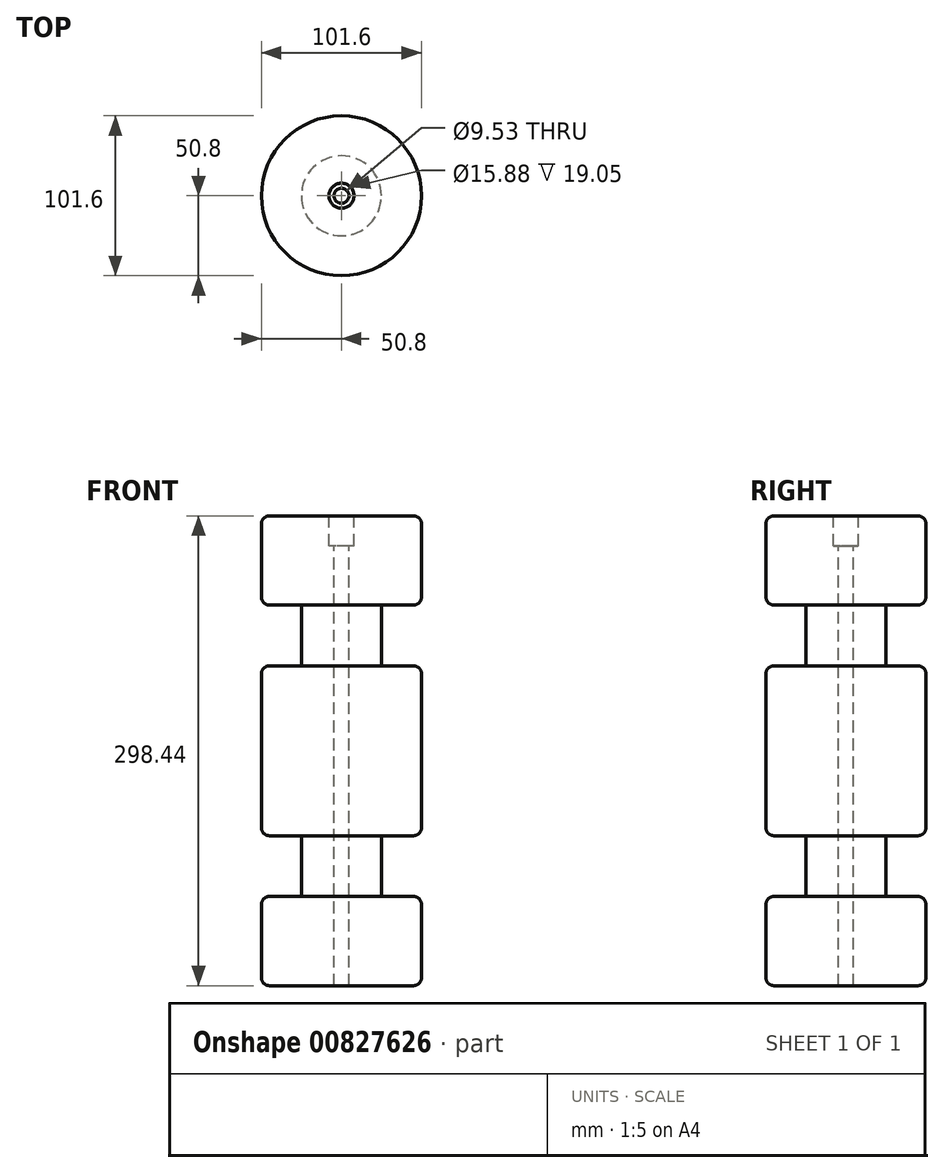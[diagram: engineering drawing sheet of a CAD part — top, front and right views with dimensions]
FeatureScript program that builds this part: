
annotation { "Feature Type Name" : "Feature", "Feature Type Description" : "" }
export const myFeature = defineFeature(function(context is Context, id is Id, definition is map)
    precondition{}
    {
        {
            var Q0;
            Q0=qCreatedBy(makeId("Front.planeOp"),FACE);
            var sketch = newSketch(context, id + "F0", { "sketchPlane" : qUnion([Q0])});
            skLineSegment(sketch, "E0.bottom", {"start": v(50.8, -53.98) * mm, "end": v(0, -53.98) * mm});
            skLineSegment(sketch, "E0.top", {"start": v(50.8, 149.22) * mm, "end": v(0, 149.22) * mm});
            skLineSegment(sketch, "E0.left", {"start": v(50.8, -53.98) * mm, "end": v(50.8, 16.34) * mm});
            skLineSegment(sketch, "E0.right", {"start": v(0, -53.98) * mm, "end": v(0, 149.22) * mm});
            skLineSegment(sketch, "E1.bottom", {"start": v(50.8, 92.54) * mm, "end": v(25.4, 92.54) * mm});
            skLineSegment(sketch, "E1.top", {"start": v(50.8, 16.34) * mm, "end": v(25.4, 16.34) * mm});
            skLineSegment(sketch, "E1.right", {"start": v(25.4, 92.54) * mm, "end": v(25.4, 16.34) * mm});
            skLineSegment(sketch, "E2.trimOffspring", {"start": v(50.8, 92.54) * mm, "end": v(50.8, 149.22) * mm});
            skSolve(sketch);
        }
        {
            var Q0;
            Q0=makeQuery(id+"F0.imprint","IMPRINT",FACE,{"disambiguationData":[TD([[makeQuery(id+"F0.imprint","IMPRINT",EDGE,{"derivedFrom":sQuery(id+"F0.wireOp",EDGE,"E0.bottom")}),-1.0]])]});
            var Q1;
            Q1=sQuery(id+"F0.wireOp",EDGE,"E0.right");
            revolve(context, id + "F1", {"surfaceOperationType" : NewSurfaceOperationType.NEW, "entities" : qUnion([Q0]), "axis" : qUnion([Q1]), "revolveType" : RevolveType.FULL});
        }
        {
            var Q0;
            Q0=makeQuery(id+"F1.opRevolve","SWEPT_EDGE",EDGE,{"disambiguationData":[OSD([sQuery(id+"F0.wireOp",EDGE,"E0.bottom"),sQuery(id+"F0.wireOp",EDGE,"E0.left")])]});
            var Q1;
            Q1=makeQuery(id+"F1.opRevolve","SWEPT_EDGE",EDGE,{"disambiguationData":[OSD([sQuery(id+"F0.wireOp",EDGE,"E0.left"),sQuery(id+"F0.wireOp",EDGE,"E1.top")])]});
            var Q2;
            Q2=makeQuery(id+"F1.opRevolve","SWEPT_EDGE",EDGE,{"disambiguationData":[OSD([sQuery(id+"F0.wireOp",EDGE,"E0.top"),sQuery(id+"F0.wireOp",EDGE,"E2.trimOffspring")])]});
            var Q3;
            Q3=makeQuery(id+"F1.opRevolve","SWEPT_EDGE",EDGE,{"disambiguationData":[OSD([sQuery(id+"F0.wireOp",EDGE,"E1.bottom"),sQuery(id+"F0.wireOp",EDGE,"E2.trimOffspring")])]});
            fillet(context, id + "F2", {"entities" : qUnion([Q0, Q1, Q2, Q3]), "radius" : 5.08 * mm, "tangentPropagation" : true, "allowEdgeOverflow" : false});
        }
        {
            var Q0;
            Q0=makeQuery(id+"F1.opRevolve","SWEPT_BODY",BODY,{"disambiguationData":[OSD([sQuery(id+"F0.wireOp",EDGE,"E0.bottom"),sQuery(id+"F0.wireOp",EDGE,"E0.top"),sQuery(id+"F0.wireOp",EDGE,"E0.left"),sQuery(id+"F0.wireOp",EDGE,"E0.right"),sQuery(id+"F0.wireOp",EDGE,"E1.bottom"),sQuery(id+"F0.wireOp",EDGE,"E1.top"),sQuery(id+"F0.wireOp",EDGE,"E1.right"),sQuery(id+"F0.wireOp",EDGE,"E2.trimOffspring")])]});
            var Q1;
            Q1=qCreatedBy(makeId("Top.planeOp"),FACE);
            mirror(context, id + "F3", {"operationType" : NewBodyOperationType.ADD, "entities" : qUnion([Q0]), "mirrorPlane" : qUnion([Q1])});
        }
        {
            var Q0;
            Q0=makeQuery(id+"F1.opRevolve","SWEPT_FACE",FACE,{"disambiguationData":[OSD([sQuery(id+"F0.wireOp",EDGE,"E0.top")])]});
            var sketch = newSketch(context, id + "F4", { "sketchPlane" : qUnion([Q0])});
            skCircle(sketch, "E3.0", {"center": v(0, 0) * mm, "radius": 45.72 * mm});
            skSolve(sketch);
        }
        {
            var Q0;
            Q0=sQuery(id+"F4.wireOp",VERTEX,"E3.0.center");
            var Q1;
            Q1=makeQuery(id+"F1.opRevolve","SWEPT_BODY",BODY,{"disambiguationData":[OSD([sQuery(id+"F0.wireOp",EDGE,"E0.bottom"),sQuery(id+"F0.wireOp",EDGE,"E0.top"),sQuery(id+"F0.wireOp",EDGE,"E0.left"),sQuery(id+"F0.wireOp",EDGE,"E0.right"),sQuery(id+"F0.wireOp",EDGE,"E1.bottom"),sQuery(id+"F0.wireOp",EDGE,"E1.top"),sQuery(id+"F0.wireOp",EDGE,"E1.right"),sQuery(id+"F0.wireOp",EDGE,"E2.trimOffspring")])]});
            hole(context, id + "F5", {"style" : HoleStyle.C_BORE, "endStyle" : HoleEndStyle.THROUGH, "standardTappedOrClearance" : lookupTablePath({ "standard" : "Custom", "fit" : "Normal", "size" : "1/4", "type" : "Clearance" }), "standardBlindInLast" : lookupTablePath({ "fit" : "Free", "standard" : "Custom", "size" : "1/4", "type" : "Clearance" }), "holeDiameter" : 9.52 * mm, "cBoreDiameter" : 15.88 * mm, "cBoreDepth" : 19.05 * mm, "majorDiameter" : 6.35 * mm, "isTappedThrough" : true, "tappedDepth" : 12.7 * mm, "tapClearance" : 3, "locations" : qUnion([Q0]), "scope" : qUnion([Q1])});
        }
    });
